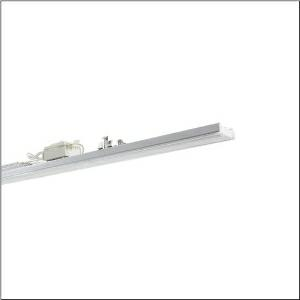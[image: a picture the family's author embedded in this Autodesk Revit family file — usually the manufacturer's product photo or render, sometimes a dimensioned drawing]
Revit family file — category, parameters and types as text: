
# Revit family: licross_r__21_recessed_ho_52tl12dn4fxm3s4_75bd
name_source: partatom
category: Lighting Fixtures
units: mm (PartAtom-declared; Revit-internal decimal feet)

## family parameters
Cut with Voids When Loaded = No
Host = Face
Light Source = No
Part Type = Normal
Room Calculation Point = No
Round Connector Dimension = Use Diameter
Shared = No

## types (1)
- --- (1 x LED, 930 lm, 7.5 W, 4000K)
    Apparent Load = 8 VA
    CIE Flux Codes = 69 91 98 100 100
    Color Rendering = 80
    Color Temperature = 4000K
    Default Elevation = 1800 mm
    Description = Licross® 21 Recessed HO, luminaire insert, of sheet steel, galvanised, coil coated, white, length: 1.500mm, width: 66mm, height: 67mm, LED rated luminous flux: 15.000lm, light colour: 840, control gear: DALI 2, with plug, 6-pole, with phase selection, for trunking rail, 9 or 11-core, mains connection: 220..240V, AC, 50/60Hz, rated input power: 88W, halogen-free wiring, for emergency light function, for trunking rail, 9-/11-core, converter,control gear: single battery element, battery: LiFePO4, 9Ah, primary optical cover: cover, of PMMA, light emission: direct distribution, primary light characteristic: symmetric, protection rating (complete): IP40, insulation class (complete): insulation class I (protective earthing), certification: CE, UKCA, protection symbol: D if used in an environment without relevant dust loads with corresponding accessories, impact resistance: IK06, permissible ambient temperature for indoor applications: +5..+35°C, standard: EN 60598-2-22, LABS conformity tested according to VDMA 24364:2018-05, reducing of maximum allowable ambient temperature of 5°C with ceiling mounting, corresponds to IFS (International Featured Standards) requirements for safety and quality in the food industry, packaging unit: 1 piece
    Height = 58 mm
    Lamp = 1 x LED
    Lamp Light Flux = 930 lm
    Lamp Power = 7.5 W
    Lamp count = 1
    Length = 1500 mm
    Luminous efficacy = 124 lm/W
    Manufacturer = Siteco
    ModVariant = No
    Model = 52TL12DN4FXM3S4
    Mounting Place = Ceiling
    Mounting Type = Pendant
    Number of Poles = 1
    OnlyDefault = Yes
    Power Factor = 1
    Product Name = Licross® 21 Recessed HO
    Product group = luminaire insert
    ProductGroupID = 902
    Protection Class = Protection class I
    Protection Degree = IP 40
    RLX_Detail_Level = 1
    RLX_Emergency_Light_Flux = 0 lm
    RLX_Emergency_Type = 0
    RLX_Emergency_Type_DB = No
    RlxData = <blob elided: 25125 chars, md5=388f0c61>
    Socket = socket
    Standby Power = 0 W
    System Light Flux = 930 lm
    System Power = 8 W
    Type Comments = : emergency light operation: 3 h
    Type Image = l_1296930.jpg
    URL = http://relux.com
    VarID = @adj_109316
    Voltage = 0 V
    Weight = 0.00 kg
    Width = 66 mm

## geometry (parser evidence)
native form markers: Blend x4, Sweep x12
no freeform markers — native parametric forms only
